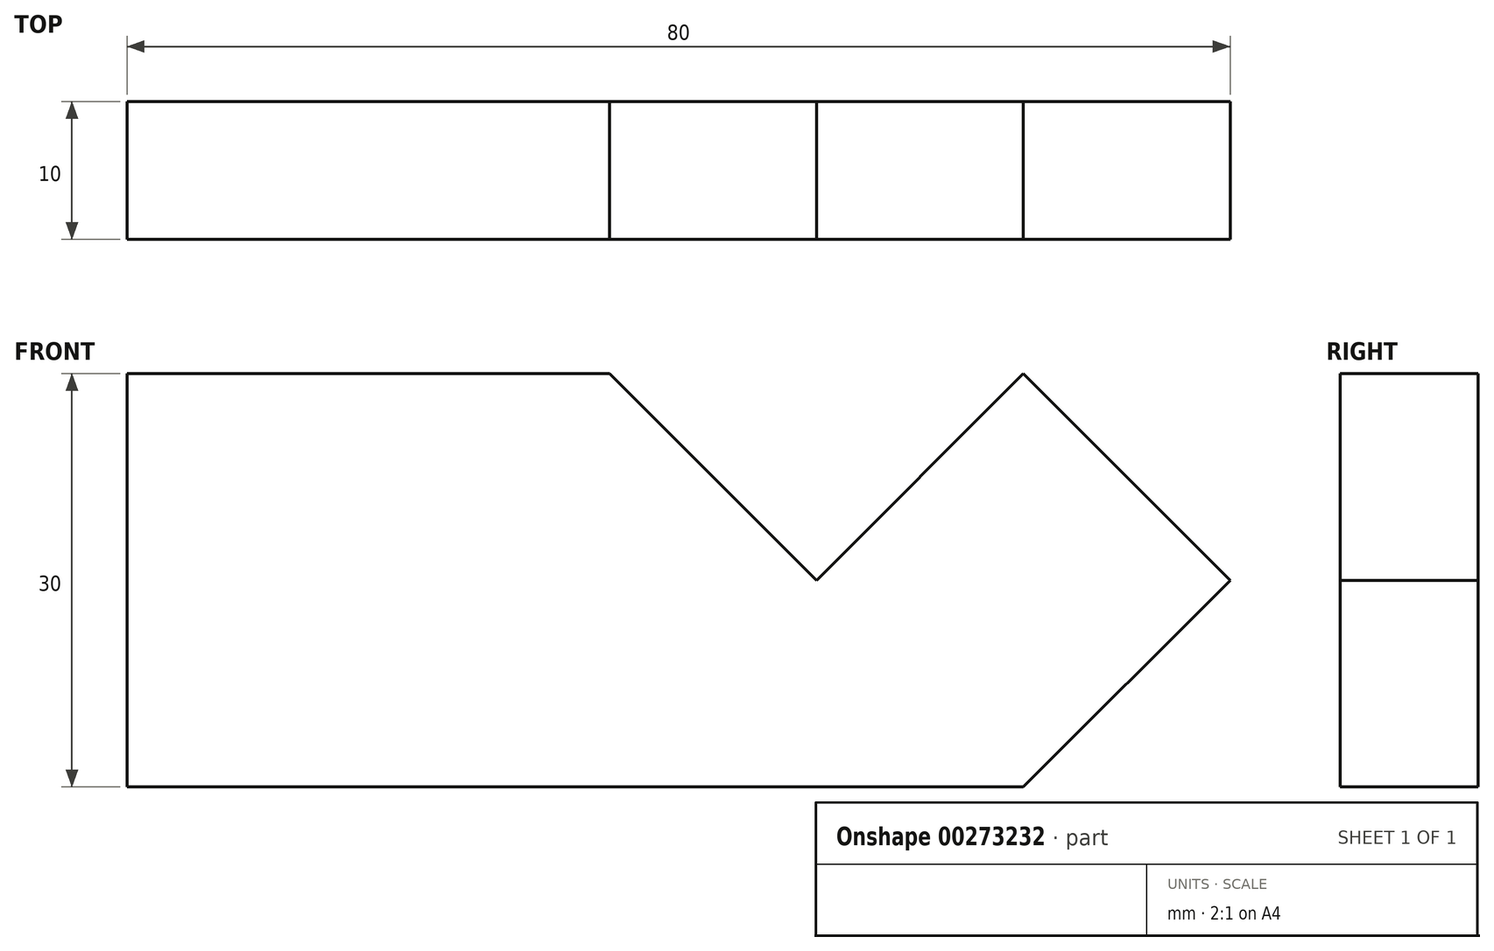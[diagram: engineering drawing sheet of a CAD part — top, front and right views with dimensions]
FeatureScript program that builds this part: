
annotation { "Feature Type Name" : "Feature", "Feature Type Description" : "" }
export const myFeature = defineFeature(function(context is Context, id is Id, definition is map)
    precondition{}
    {
        {
            var Q0;
            Q0=qCreatedBy(makeId("Front.planeOp"),FACE);
            var sketch = newSketch(context, id + "F0", { "sketchPlane" : qUnion([Q0])});
            skLineSegment(sketch, "E0", {"start": v(80, 15) * mm, "end": v(65, 0) * mm});
            skLineSegment(sketch, "E1", {"start": v(0, 0) * mm, "end": v(0, 30) * mm});
            skLineSegment(sketch, "E2", {"start": v(35, 30) * mm, "end": v(50, 15) * mm});
            skLineSegment(sketch, "E3", {"start": v(50, 15) * mm, "end": v(65, 30) * mm});
            skLineSegment(sketch, "E4", {"start": v(65, 30) * mm, "end": v(80, 15) * mm});
            skLineSegment(sketch, "E5", {"start": v(0, 30) * mm, "end": v(35, 30) * mm});
            skLineSegment(sketch, "E6", {"start": v(0, 0) * mm, "end": v(65, 0) * mm});
            skSolve(sketch);
        }
        {
            var Q0;
            Q0=makeQuery(id+"F0.imprint","IMPRINT",FACE,{"disambiguationData":[TD([[makeQuery(id+"F0.imprint","IMPRINT",EDGE,{"derivedFrom":sQuery(id+"F0.wireOp",EDGE,"E0")}),-1.0]])]});
            extrude(context, id + "F1", {"entities" : qUnion([Q0]), "depth" : 10 * mm});
        }
    });
